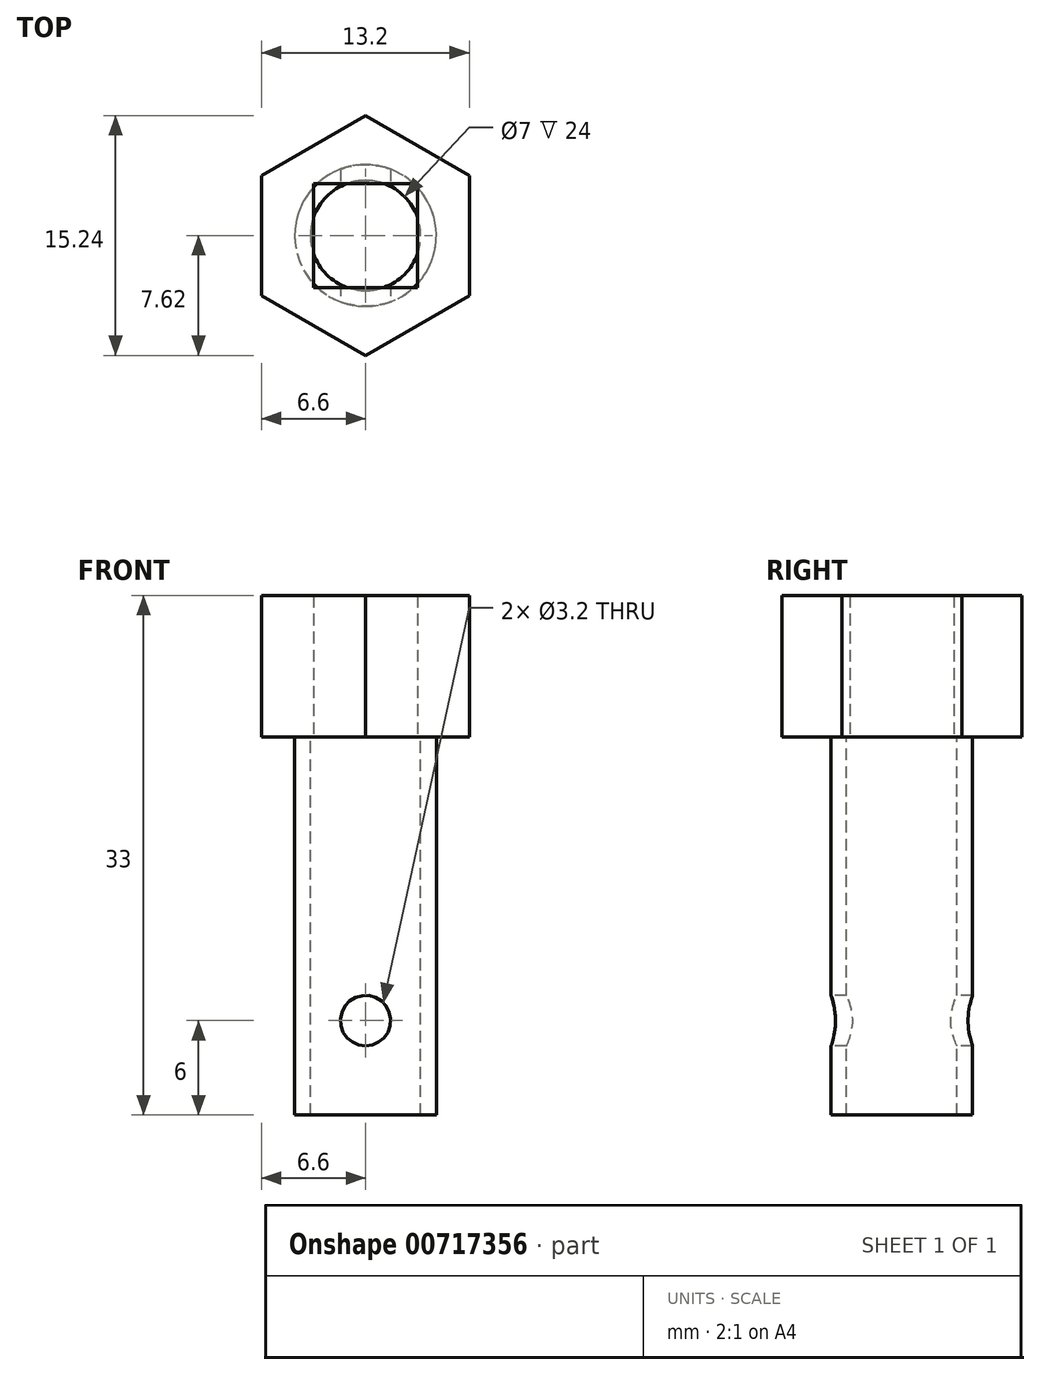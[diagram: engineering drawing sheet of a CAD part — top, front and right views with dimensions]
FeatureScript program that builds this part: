
annotation { "Feature Type Name" : "Feature", "Feature Type Description" : "" }
export const myFeature = defineFeature(function(context is Context, id is Id, definition is map)
    precondition{}
    {
        {
            var Q0;
            Q0=qCreatedBy(makeId("Top.planeOp"),FACE);
            var sketch = newSketch(context, id + "F0", { "sketchPlane" : qUnion([Q0])});
            skLineSegment(sketch, "E0", {"start": v(0, 0) * mm, "end": v(-3.3, 0) * mm});
            skLineSegment(sketch, "E1", {"start": v(-3.3, 0) * mm, "end": v(-3.3, 3.3) * mm});
            skLineSegment(sketch, "E2", {"start": v(0, 0) * mm, "end": v(0, 1.74) * mm});
            skLineSegment(sketch, "E3", {"start": v(-3.3, 3.3) * mm, "end": v(0, 3.3) * mm});
            skPoint(sketch, "E3.endSnap0", {"position": v(0, 0.87) * mm});
            skLineSegment(sketch, "E4.MirrorCS", {"start": v(3.3, 0) * mm, "end": v(3.3, 3.3) * mm});
            skLineSegment(sketch, "E5.MirrorCS", {"start": v(3.3, 3.3) * mm, "end": v(0, 3.3) * mm});
            skLineSegment(sketch, "E6.MirrorCS", {"start": v(-3.3, 0) * mm, "end": v(-3.3, -3.3) * mm});
            skLineSegment(sketch, "E7.MirrorCS", {"start": v(-3.3, -3.3) * mm, "end": v(0, -3.3) * mm});
            skLineSegment(sketch, "E8.MirrorCS", {"start": v(3.3, -3.3) * mm, "end": v(0, -3.3) * mm});
            skLineSegment(sketch, "E9.MirrorCS", {"start": v(3.3, 0) * mm, "end": v(3.3, -3.3) * mm});
            skCircle(sketch, "E10.cCircle", {"center": v(0, 0) * mm, "radius": 6.6 * mm, "construction": true});
            skLineSegment(sketch, "E10.0", {"start": v(6.6, 3.81) * mm, "end": v(6.6, -3.81) * mm});
            skLineSegment(sketch, "E10.1", {"start": v(6.6, -3.81) * mm, "end": v(0, -7.62) * mm});
            skLineSegment(sketch, "E10.2", {"start": v(0, -7.62) * mm, "end": v(-6.6, -3.81) * mm});
            skLineSegment(sketch, "E10.3", {"start": v(-6.6, -3.81) * mm, "end": v(-6.6, 3.81) * mm});
            skLineSegment(sketch, "E10.4", {"start": v(-6.6, 3.81) * mm, "end": v(0, 7.62) * mm});
            skLineSegment(sketch, "E10.5", {"start": v(0, 7.62) * mm, "end": v(6.6, 3.81) * mm});
            skPoint(sketch, "E10.0.midPoint", {"position": v(6.6, 0) * mm});
            skSolve(sketch);
        }
        {
            var Q0;
            Q0=qSketchRegion(id+"F0",true);
            extrude(context, id + "F1", {"entities" : qUnion([Q0]), "depth" : 9 * mm, "offsetDistance" : 25 * mm});
        }
        {
            var Q0;
            Q0=makeQuery(id+"F1.opExtrude","SWEPT_FACE",FACE,{"disambiguationData":[OSD([sQuery(id+"F0.wireOp",EDGE,"E10.3")])]});
            var sketch = newSketch(context, id + "F2", { "sketchPlane" : qUnion([Q0])});
            skLineSegment(sketch, "E11", {"start": v(0, 9) * mm, "end": v(0, -12) * mm});
            skCircle(sketch, "E12", {"center": v(0, -12) * mm, "radius": 1.6 * mm});
            skSolve(sketch);
        }
        {
            var Q0;
            Q0=makeQuery(id+"F2.imprint","IMPRINT",FACE,{"disambiguationData":[TD([[makeQuery(id+"F2.imprint","IMPRINT",EDGE,{"derivedFrom":sQuery(id+"F2.wireOp",EDGE,"E12")}),1.0]])]});
            extrude(context, id + "F3", {"entities" : qUnion([Q0]), "operationType" : NewBodyOperationType.REMOVE, "oppositeDirection" : true, "depth" : 25 * mm, "offsetDistance" : 25 * mm});
        }
        {
            var Q0;
            Q0=makeQuery(id+"F1.opExtrude","CAP_FACE",FACE,{"disambiguationData":[OSD([sQuery(id+"F0.wireOp",EDGE,"E1"),sQuery(id+"F0.wireOp",EDGE,"E3"),sQuery(id+"F0.wireOp",EDGE,"E4.MirrorCS"),sQuery(id+"F0.wireOp",EDGE,"E5.MirrorCS"),sQuery(id+"F0.wireOp",EDGE,"E6.MirrorCS"),sQuery(id+"F0.wireOp",EDGE,"E7.MirrorCS"),sQuery(id+"F0.wireOp",EDGE,"E8.MirrorCS"),sQuery(id+"F0.wireOp",EDGE,"E9.MirrorCS"),sQuery(id+"F0.wireOp",EDGE,"E10.0"),sQuery(id+"F0.wireOp",EDGE,"E10.1"),sQuery(id+"F0.wireOp",EDGE,"E10.2"),sQuery(id+"F0.wireOp",EDGE,"E10.3"),sQuery(id+"F0.wireOp",EDGE,"E10.4"),sQuery(id+"F0.wireOp",EDGE,"E10.5")])],"isStart":true});
            var sketch = newSketch(context, id + "F4", { "sketchPlane" : qUnion([Q0])});
            skCircle(sketch, "E13", {"center": v(0, 0) * mm, "radius": 3.5 * mm});
            skCircle(sketch, "E14", {"center": v(0, 0) * mm, "radius": 4.5 * mm});
            skSolve(sketch);
        }
        {
            var Q0;
            Q0=qSketchRegion(id+"F4",true);
            extrude(context, id + "F5", {"entities" : qUnion([Q0]), "operationType" : NewBodyOperationType.ADD, "depth" : 24 * mm, "offsetDistance" : 25 * mm});
        }
        {
            var Q0;
            Q0=makeQuery(id+"F1.opExtrude","SWEPT_FACE",FACE,{"disambiguationData":[OSD([sQuery(id+"F0.wireOp",EDGE,"E7.MirrorCS"),sQuery(id+"F0.wireOp",EDGE,"E8.MirrorCS")])]});
            var sketch = newSketch(context, id + "F6", { "sketchPlane" : qUnion([Q0])});
            skLineSegment(sketch, "E15", {"start": v(0, 9) * mm, "end": v(0, -18) * mm});
            skCircle(sketch, "E16", {"center": v(0, -18) * mm, "radius": 1.6 * mm});
            skSolve(sketch);
        }
        {
            var Q0;
            Q0=qSketchRegion(id+"F6",true);
            extrude(context, id + "F7", {"entities" : qUnion([Q0]), "operationType" : NewBodyOperationType.REMOVE, "depth" : 25 * mm, "offsetDistance" : 25 * mm, "hasSecondDirection" : true, "secondDirectionOppositeDirection" : true, "secondDirectionDepth" : 25 * mm});
        }
    });
